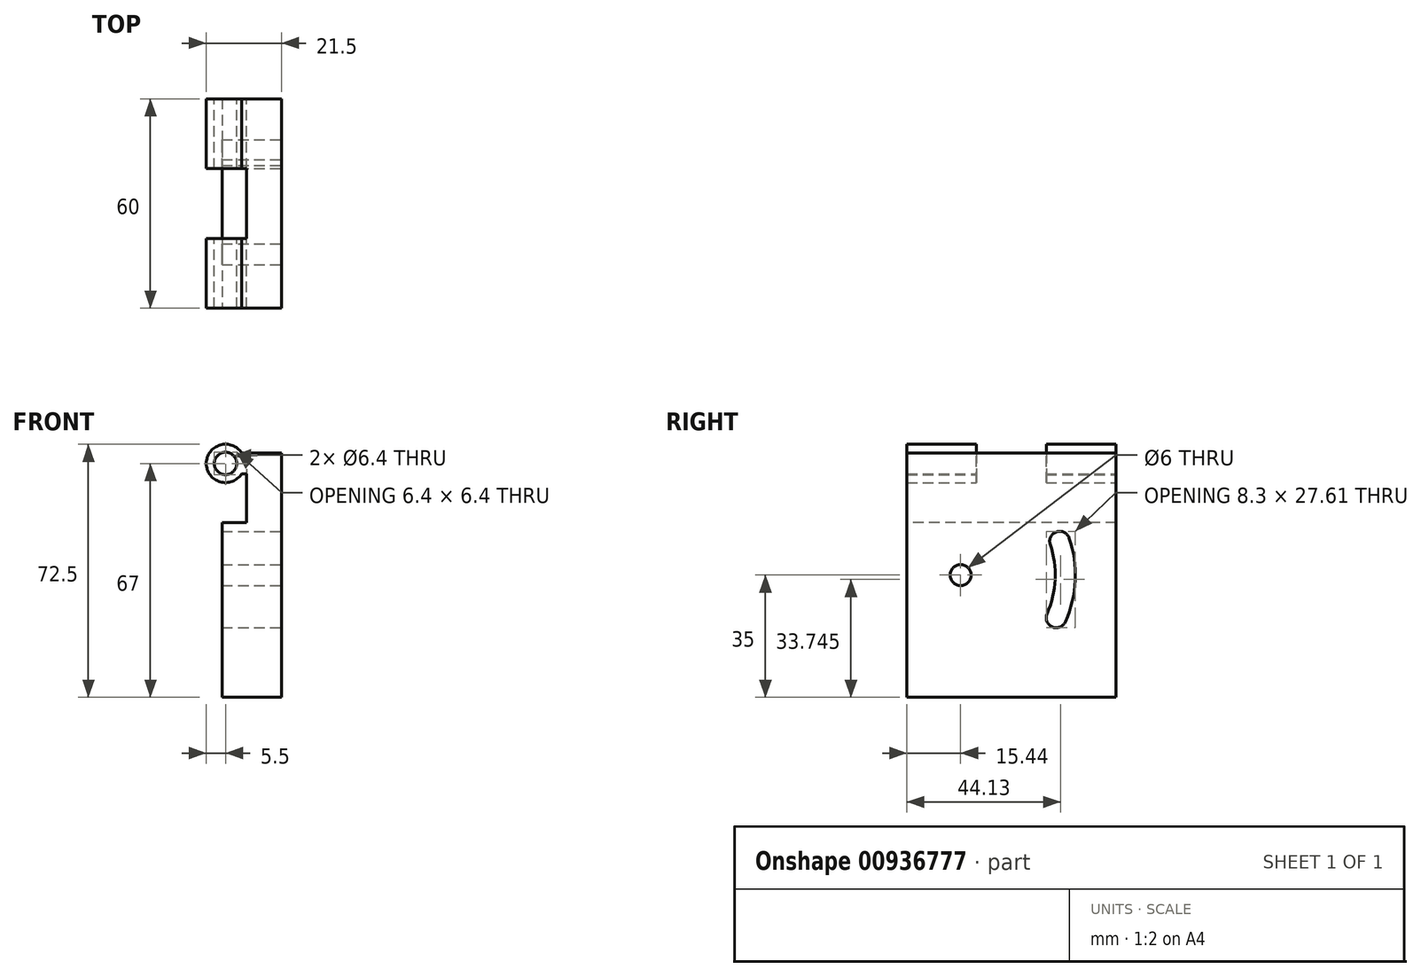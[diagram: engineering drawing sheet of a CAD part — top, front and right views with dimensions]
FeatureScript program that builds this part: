
annotation { "Feature Type Name" : "Feature", "Feature Type Description" : "" }
export const myFeature = defineFeature(function(context is Context, id is Id, definition is map)
    precondition{}
    {
        {
            var Q0;
            Q0=qCreatedBy(makeId("Front.planeOp"),FACE);
            var sketch = newSketch(context, id + "F0", { "sketchPlane" : qUnion([Q0])});
            skLineSegment(sketch, "E0", {"start": v(-10, 0) * mm, "end": v(0, 0) * mm});
            skLineSegment(sketch, "E1", {"start": v(0, 0) * mm, "end": v(0, 70) * mm});
            skLineSegment(sketch, "E2", {"start": v(0, 70) * mm, "end": v(-11.4, 70) * mm});
            skLineSegment(sketch, "E3", {"start": v(-11.4, 64) * mm, "end": v(-10, 64) * mm});
            skLineSegment(sketch, "E4", {"start": v(-10, 64) * mm, "end": v(-10, 0) * mm});
            skArc(sketch, "E5", {"start": v(-11.4, 70) * mm, "mid": v(-21.5, 67) * mm, "end": v(-11.4, 64) * mm});
            skPoint(sketch, "E5.centerSnap0", {"position": v(-11.4, 67) * mm});
            skCircle(sketch, "E6", {"center": v(-16, 67) * mm, "radius": 3.2 * mm});
            skSolve(sketch);
        }
        {
            var Q0;
            Q0 = qSketchRegion(id + "F0", true);
            extrude(context, id + "F1", {"entities" : qUnion([Q0]), "depth" : 60 * mm, "offsetDistance" : 25 * mm});
        }
        {
            var Q0;
            Q0=qCreatedBy(makeId("Top.planeOp"),FACE);
            var sketch = newSketch(context, id + "F2", { "sketchPlane" : qUnion([Q0])});
            skLineSegment(sketch, "E7.bottom", {"start": v(-33.02, -20) * mm, "end": v(-10, -20) * mm});
            skLineSegment(sketch, "E7.top", {"start": v(-33.02, -40) * mm, "end": v(-10, -40) * mm});
            skLineSegment(sketch, "E7.left", {"start": v(-33.02, -20) * mm, "end": v(-33.02, -40) * mm});
            skLineSegment(sketch, "E8", {"start": v(-10, -20) * mm, "end": v(-10, -40) * mm});
            skSolve(sketch);
        }
        {
            var Q0;
            Q0 = qSketchRegion(id + "F2", true);
            extrude(context, id + "F3", {"entities" : qUnion([Q0]), "operationType" : NewBodyOperationType.REMOVE, "endBound" : BoundingType.THROUGH_ALL, "depth" : 51.6 * mm, "offsetDistance" : 25 * mm});
        }
        {
            var Q0;
            Q0=qCreatedBy(makeId("Top.planeOp"),FACE);
            var sketch = newSketch(context, id + "F4", { "sketchPlane" : qUnion([Q0])});
            skLineSegment(sketch, "E9.bottom", {"start": v(0, 0) * mm, "end": v(-17, 0) * mm});
            skLineSegment(sketch, "E9.top", {"start": v(0, -60) * mm, "end": v(-17, -60) * mm});
            skLineSegment(sketch, "E9.left", {"start": v(0, 0) * mm, "end": v(0, -60) * mm});
            skLineSegment(sketch, "E9.right", {"start": v(-17, 0) * mm, "end": v(-17, -60) * mm});
            skSolve(sketch);
        }
        {
            var Q0;
            Q0 = qSketchRegion(id + "F4", true);
            extrude(context, id + "F5", {"entities" : qUnion([Q0]), "operationType" : NewBodyOperationType.ADD, "depth" : 50 * mm, "offsetDistance" : 25 * mm});
        }
        {
            var Q0;
            Q0=makeQuery(id+"F1.opExtrude","SWEPT_FACE",FACE,{"disambiguationData":[OSD([sQuery(id+"F0.wireOp",EDGE,"E1")])]});
            var sketch = newSketch(context, id + "F6", { "sketchPlane" : qUnion([Q0])});
            skCircle(sketch, "E10", {"center": v(-44.56, 35) * mm, "radius": 3 * mm});
            skArc(sketch, "E11", {"start": v(-19.77, 23.98) * mm, "mid": v(-17.46, 33.78) * mm, "end": v(-18.89, 43.76) * mm});
            skArc(sketch, "E12", {"start": v(-14.52, 21.64) * mm, "mid": v(-11.72, 33.53) * mm, "end": v(-13.45, 45.61) * mm});
            skArc(sketch, "E13", {"start": v(-13.45, 45.61) * mm, "mid": v(-17.1, 47.4) * mm, "end": v(-18.89, 43.76) * mm});
            skArc(sketch, "E14", {"start": v(-19.77, 23.98) * mm, "mid": v(-18.31, 20.19) * mm, "end": v(-14.52, 21.64) * mm});
            skPoint(sketch, "E15.center.orphan", {"position": v(-14.56, 35) * mm});
            skSolve(sketch);
        }
        {
            var Q0;
            Q0 = qSketchRegion(id + "F6", true);
            extrude(context, id + "F7", {"entities" : qUnion([Q0]), "operationType" : NewBodyOperationType.REMOVE, "oppositeDirection" : true, "depth" : 25 * mm, "offsetDistance" : 25 * mm});
        }
    });
